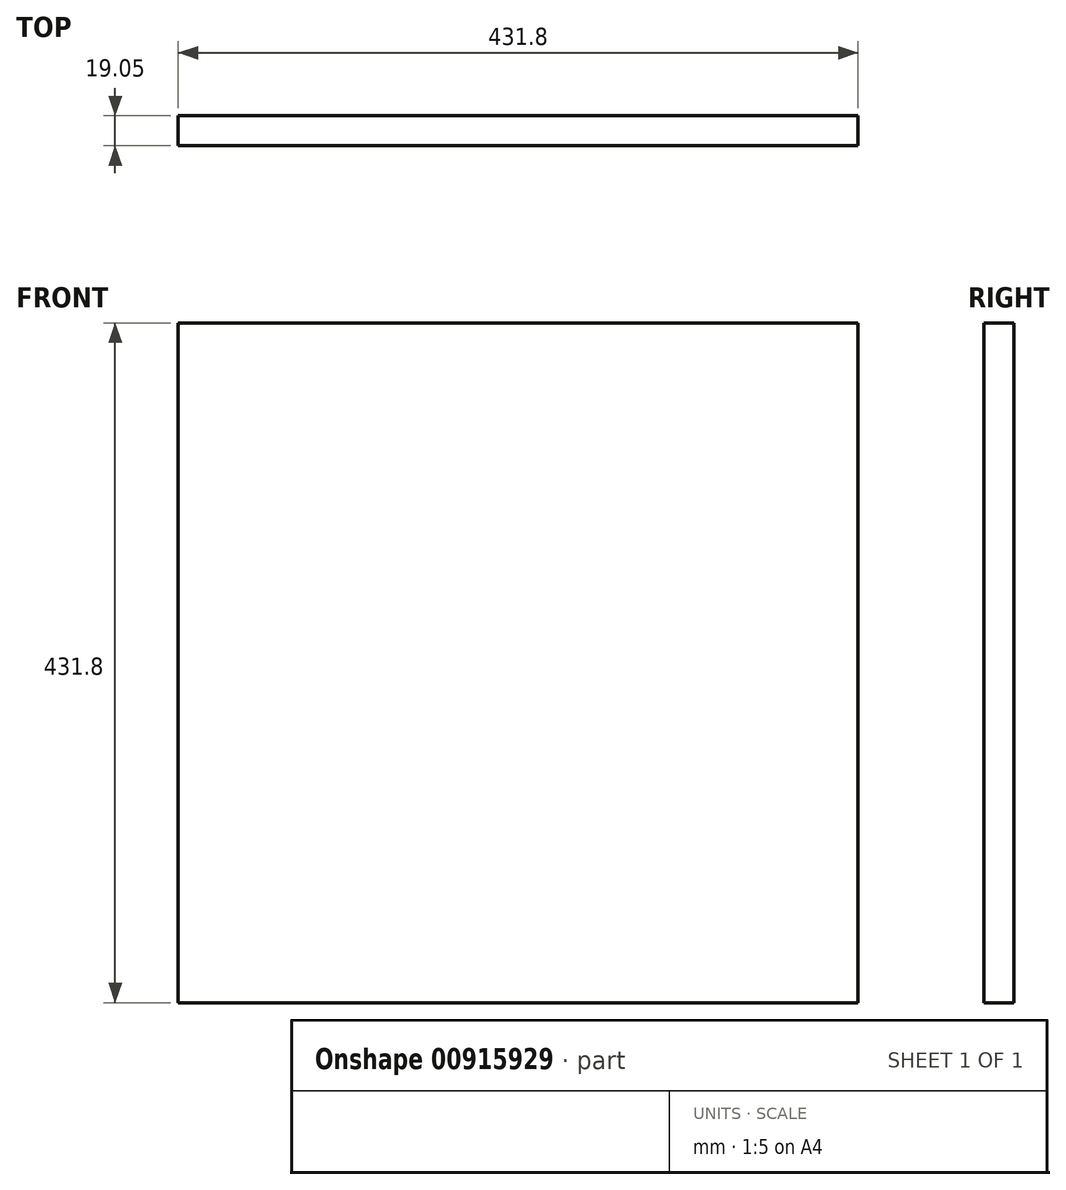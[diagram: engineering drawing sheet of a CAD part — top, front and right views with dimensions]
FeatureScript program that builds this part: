
annotation { "Feature Type Name" : "Feature", "Feature Type Description" : "" }
export const myFeature = defineFeature(function(context is Context, id is Id, definition is map)
    precondition{}
    {
        {
            var Q0;
            Q0=qCreatedBy(makeId("Front.planeOp"),FACE);
            var sketch = newSketch(context, id + "F0", { "sketchPlane" : qUnion([Q0])});
            skLineSegment(sketch, "E0.bottom", {"start": v(0, 0) * mm, "end": v(431.8, 0) * mm});
            skLineSegment(sketch, "E0.top", {"start": v(0, 431.8) * mm, "end": v(431.8, 431.8) * mm});
            skLineSegment(sketch, "E0.left", {"start": v(0, 0) * mm, "end": v(0, 431.8) * mm});
            skLineSegment(sketch, "E0.right", {"start": v(431.8, 0) * mm, "end": v(431.8, 431.8) * mm});
            skSolve(sketch);
        }
        {
            var Q0;
            Q0=makeQuery(id+"F0.imprint","IMPRINT",FACE,{"disambiguationData":[TD([[makeQuery(id+"F0.imprint","IMPRINT",EDGE,{"derivedFrom":sQuery(id+"F0.wireOp",EDGE,"E0.bottom")}),1.0]])]});
            extrude(context, id + "F1", {"entities" : qUnion([Q0]), "depth" : 19.05 * mm, "offsetDistance" : 25.4 * mm});
        }
    });
